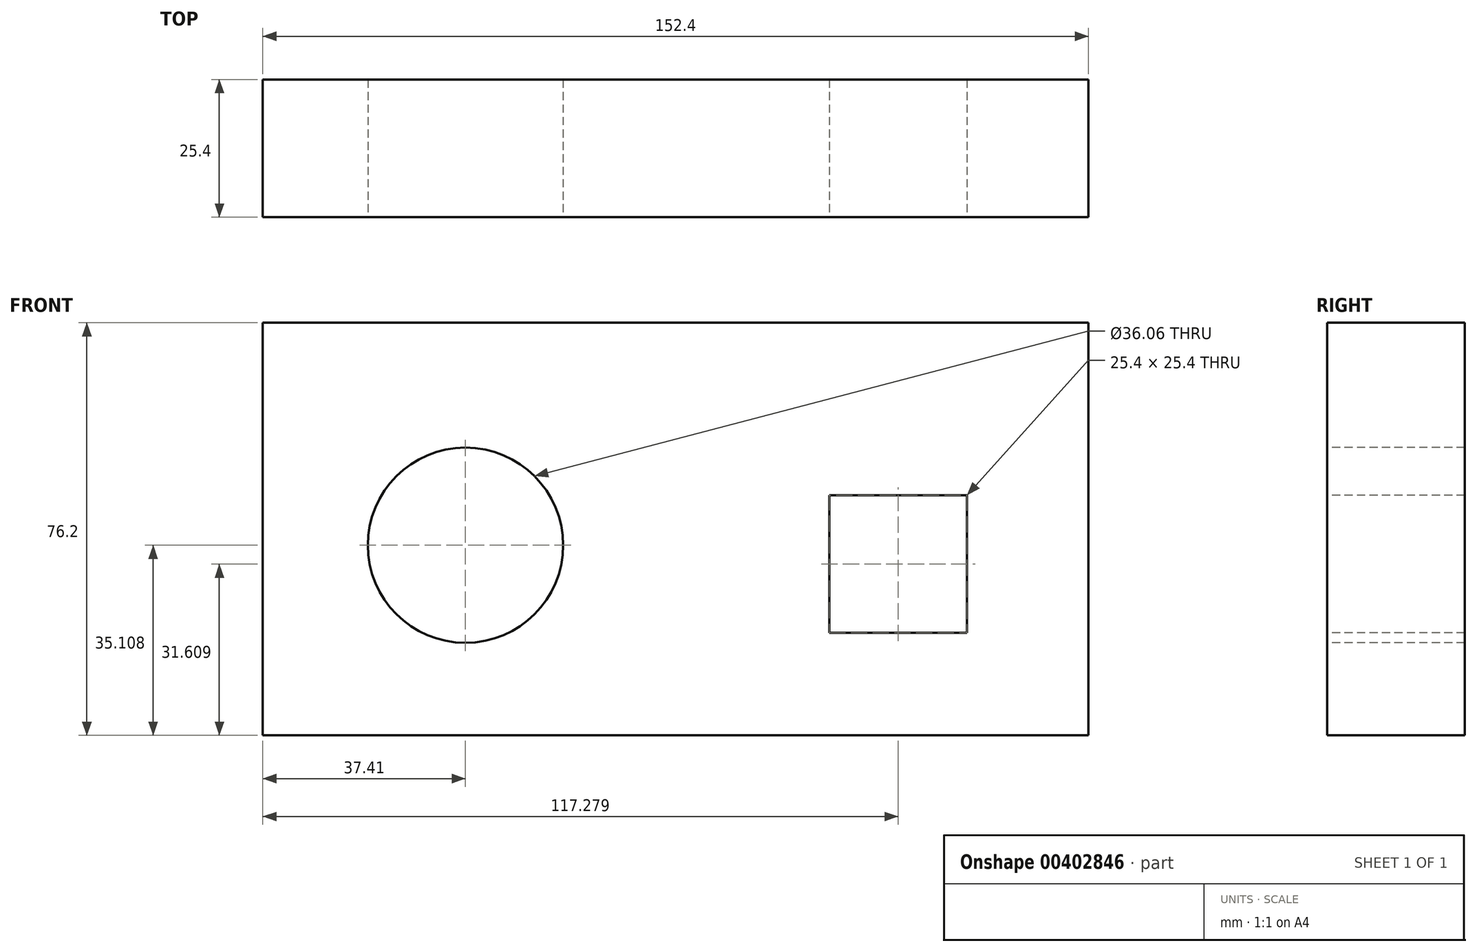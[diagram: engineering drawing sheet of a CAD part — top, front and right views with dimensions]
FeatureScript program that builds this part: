
annotation { "Feature Type Name" : "Feature", "Feature Type Description" : "" }
export const myFeature = defineFeature(function(context is Context, id is Id, definition is map)
    precondition{}
    {
        {
            var Q0;
            Q0=qCreatedBy(makeId("Front.planeOp"),FACE);
            var sketch = newSketch(context, id + "F0", { "sketchPlane" : qUnion([Q0])});
            skLineSegment(sketch, "E0", {"start": v(-76.06, 0) * mm, "end": v(76.34, 0) * mm});
            skLineSegment(sketch, "E1", {"start": v(76.34, 0) * mm, "end": v(76.34, -76.2) * mm});
            skLineSegment(sketch, "E2", {"start": v(76.34, -76.2) * mm, "end": v(-76.06, -76.2) * mm});
            skLineSegment(sketch, "E3", {"start": v(-76.06, -76.2) * mm, "end": v(-76.06, 0) * mm});
            skSolve(sketch);
        }
        {
            var Q0;
            Q0=makeQuery(id+"F0.imprint","IMPRINT",FACE,{"disambiguationData":[TD([[makeQuery(id+"F0.imprint","IMPRINT",EDGE,{"derivedFrom":sQuery(id+"F0.wireOp",EDGE,"E0")}),-1.0]])]});
            extrude(context, id + "F1", {"entities" : qUnion([Q0]), "depth" : 25.4 * mm});
        }
        {
            var Q0;
            Q0=makeQuery(id+"F1.opExtrude","CAP_FACE",FACE,{"disambiguationData":[OSD([sQuery(id+"F0.wireOp",EDGE,"E0"),sQuery(id+"F0.wireOp",EDGE,"E1"),sQuery(id+"F0.wireOp",EDGE,"E2"),sQuery(id+"F0.wireOp",EDGE,"E3")])],"isStart":false});
            var sketch = newSketch(context, id + "F2", { "sketchPlane" : qUnion([Q0])});
            skCircle(sketch, "E4", {"center": v(-38.65, -41.1) * mm, "radius": 18.03 * mm});
            skSolve(sketch);
        }
        {
            var Q0;
            Q0=makeQuery(id+"F2.imprint","IMPRINT",FACE,{"disambiguationData":[TD([[makeQuery(id+"F2.imprint","IMPRINT",EDGE,{"derivedFrom":sQuery(id+"F2.wireOp",EDGE,"E4")}),-1.0]])]});
            var sketch = newSketch(context, id + "F3", { "sketchPlane" : qUnion([Q0])});
            skLineSegment(sketch, "E5.bottom", {"start": v(53.92, -57.3) * mm, "end": v(28.52, -57.3) * mm});
            skLineSegment(sketch, "E5.top", {"start": v(53.92, -31.9) * mm, "end": v(28.52, -31.9) * mm});
            skLineSegment(sketch, "E5.left", {"start": v(53.92, -57.3) * mm, "end": v(53.92, -31.9) * mm});
            skLineSegment(sketch, "E5.right", {"start": v(28.52, -57.3) * mm, "end": v(28.52, -31.9) * mm});
            skSolve(sketch);
        }
        {
            var Q0;
            Q0=makeQuery(id+"F2.imprint","IMPRINT",FACE,{"disambiguationData":[TD([[makeQuery(id+"F2.imprint","IMPRINT",EDGE,{"derivedFrom":sQuery(id+"F2.wireOp",EDGE,"E4")}),1.0]])]});
            extrude(context, id + "F4", {"entities" : qUnion([Q0]), "operationType" : NewBodyOperationType.REMOVE, "oppositeDirection" : true, "depth" : 25.4 * mm});
        }
        {
            var Q0;
            Q0=makeQuery(id+"F3.imprint","IMPRINT",FACE,{"disambiguationData":[TD([[makeQuery(id+"F3.imprint","IMPRINT",EDGE,{"derivedFrom":sQuery(id+"F3.wireOp",EDGE,"E5.bottom")}),-1.0]])]});
            extrude(context, id + "F5", {"entities" : qUnion([Q0]), "operationType" : NewBodyOperationType.REMOVE, "oppositeDirection" : true, "depth" : 25.4 * mm});
        }
    });
